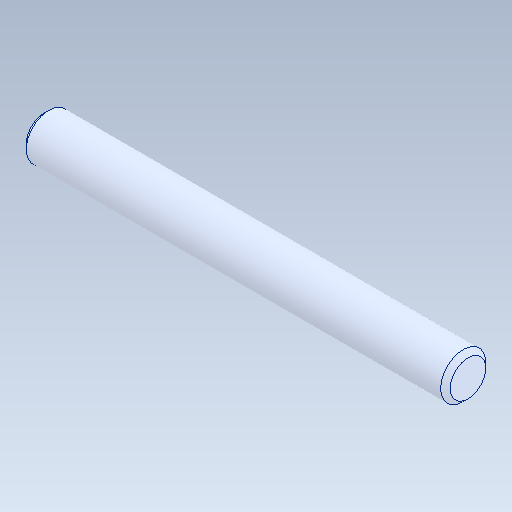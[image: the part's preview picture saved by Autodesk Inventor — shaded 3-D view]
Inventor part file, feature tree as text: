
AUTODESK INVENTOR PART (.ipt)
format: ipt  version: 2020 (Build 240168000, 168)  size: 88,064 bytes
history: native  units: in
note: dims shown in document units (in); Inventor stores cm internally (conversion verified against a paired STEP export)
features: chamfer x1
ambient origin geometry x8: Origin, YZ Plane, XZ Plane, XY Plane, X Axis, Y Axis, Z Axis, Center Point
bodies: Solid1 (feature_tree)
feature tree (1):
  chamfer  "Chamfer1"  [1 undecoded]
note: 1 required parameter value undecoded (feature->parameter linkage not recoverable at this tier; creation-order binding heuristic only, values carry confidence <= 0.55)
